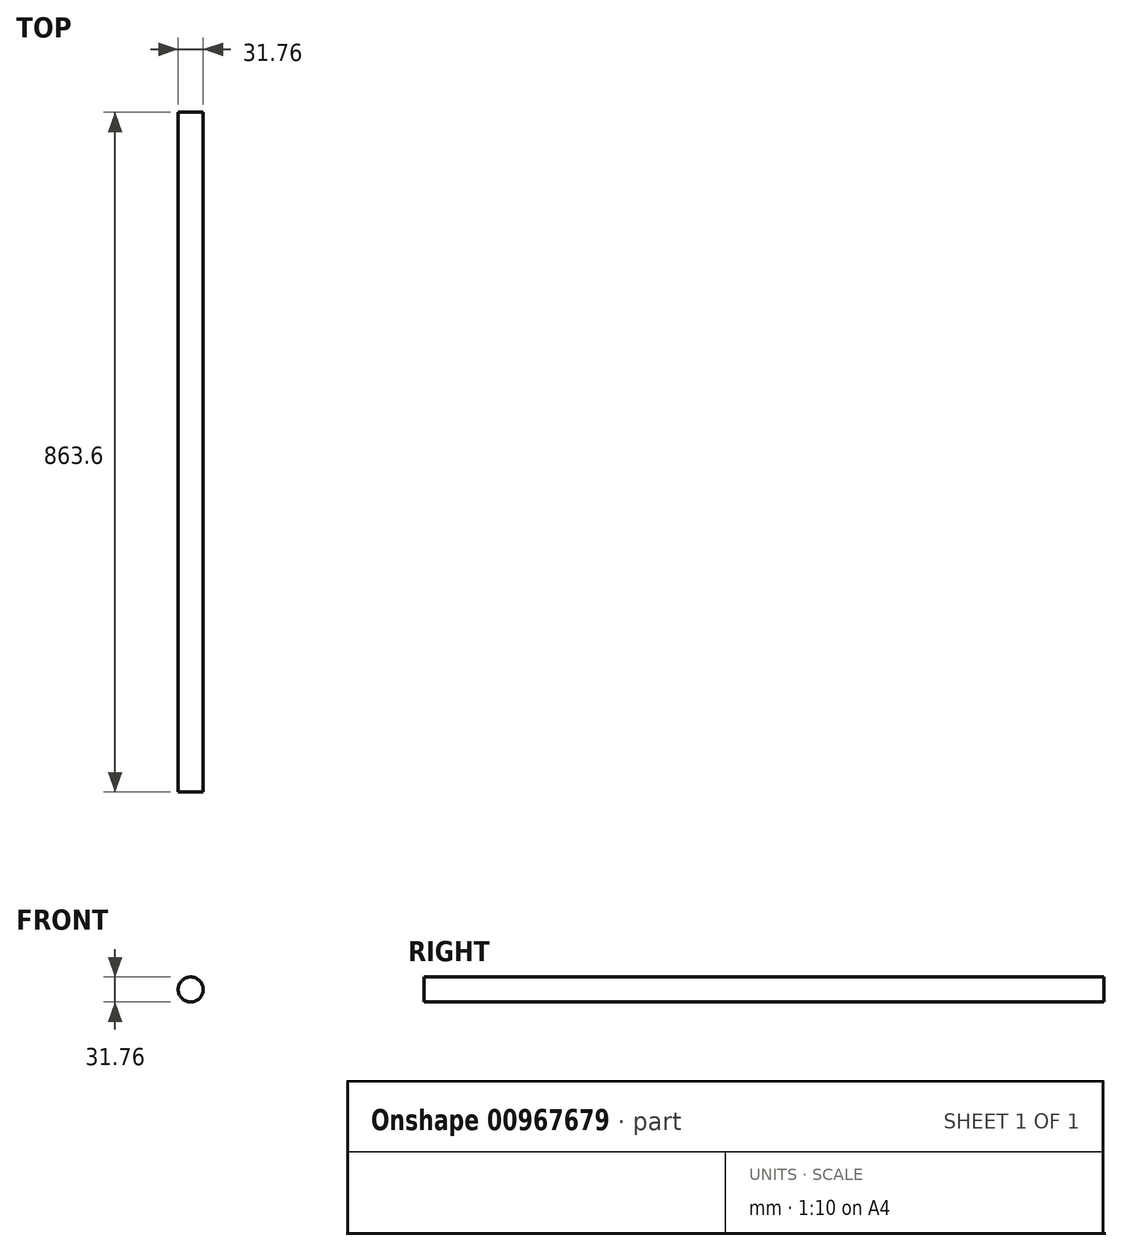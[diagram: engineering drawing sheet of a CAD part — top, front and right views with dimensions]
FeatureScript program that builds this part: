
annotation { "Feature Type Name" : "Feature", "Feature Type Description" : "" }
export const myFeature = defineFeature(function(context is Context, id is Id, definition is map)
    precondition{}
    {
        {
            var Q0;
            Q0=qCreatedBy(makeId("Front.planeOp"),FACE);
            var sketch = newSketch(context, id + "F0", { "sketchPlane" : qUnion([Q0])});
            skCircle(sketch, "E0", {"center": v(0, 0) * mm, "radius": 15.88 * mm});
            skSolve(sketch);
        }
        {
            var Q0;
            Q0=makeQuery(id+"F0.imprint","IMPRINT",FACE,{"disambiguationData":[TD([[makeQuery(id+"F0.imprint","IMPRINT",EDGE,{"derivedFrom":sQuery(id+"F0.wireOp",EDGE,"E0")}),1.0]])]});
            extrude(context, id + "F1", {"entities" : qUnion([Q0]), "depth" : 863.6 * mm, "offsetDistance" : 25.4 * mm});
        }
    });
